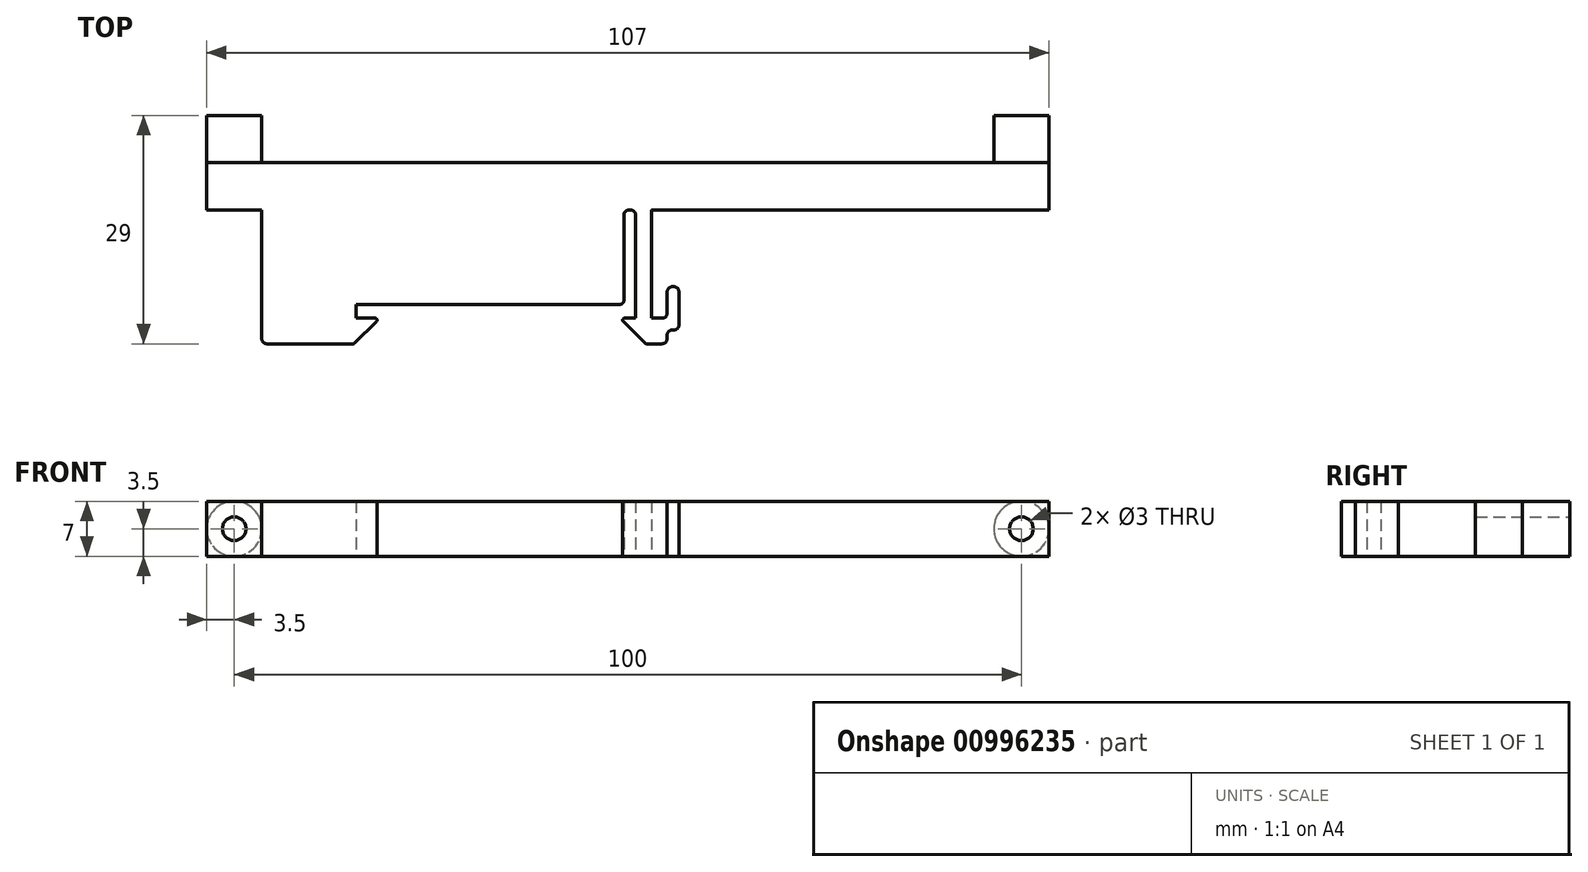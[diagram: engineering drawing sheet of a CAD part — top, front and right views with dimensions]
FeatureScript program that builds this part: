
annotation { "Feature Type Name" : "Feature", "Feature Type Description" : "" }
export const myFeature = defineFeature(function(context is Context, id is Id, definition is map)
    precondition{}
    {
        {
            var Q0;
            Q0=qCreatedBy(makeId("Top.planeOp"),FACE);
            var sketch = newSketch(context, id + "F0", { "sketchPlane" : qUnion([Q0])});
            skLineSegment(sketch, "E0", {"start": v(0, 0) * mm, "end": v(33.5, 0) * mm});
            skLineSegment(sketch, "E1", {"start": v(34, 0.5) * mm, "end": v(34, 11.35) * mm});
            skLineSegment(sketch, "E2", {"start": v(34.65, 12) * mm, "end": v(34.85, 12) * mm});
            skLineSegment(sketch, "E3", {"start": v(35.5, 11.35) * mm, "end": v(35.5, -1.75) * mm});
            skLineSegment(sketch, "E4", {"start": v(35.5, -1.75) * mm, "end": v(34.1, -1.75) * mm});
            skLineSegment(sketch, "E5", {"start": v(33.93, -2.18) * mm, "end": v(36.68, -4.93) * mm});
            skLineSegment(sketch, "E6", {"start": v(36.85, -5) * mm, "end": v(38.85, -5) * mm});
            skLineSegment(sketch, "E7", {"start": v(39.5, -4.35) * mm, "end": v(39.5, -3.9) * mm});
            skLineSegment(sketch, "E8", {"start": v(40.15, -3.25) * mm, "end": v(40.35, -3.25) * mm});
            skLineSegment(sketch, "E9", {"start": v(41, -2.6) * mm, "end": v(41, 1.6) * mm});
            skLineSegment(sketch, "E10", {"start": v(40.35, 2.25) * mm, "end": v(40.15, 2.25) * mm});
            skLineSegment(sketch, "E11", {"start": v(39.5, 1.6) * mm, "end": v(39.5, -1.1) * mm});
            skLineSegment(sketch, "E12", {"start": v(38.85, -1.75) * mm, "end": v(37.5, -1.75) * mm});
            skLineSegment(sketch, "E13", {"start": v(37.5, -1.75) * mm, "end": v(37.5, 11.96) * mm});
            skLineSegment(sketch, "E14", {"start": v(37.54, 12) * mm, "end": v(88, 12) * mm});
            skLineSegment(sketch, "E15", {"start": v(88, 12) * mm, "end": v(88, 18) * mm});
            skLineSegment(sketch, "E16", {"start": v(88, 18) * mm, "end": v(-19, 18) * mm});
            skLineSegment(sketch, "E17", {"start": v(-19, 18) * mm, "end": v(-19, 12) * mm});
            skLineSegment(sketch, "E18", {"start": v(-19, 12) * mm, "end": v(-12, 12) * mm});
            skLineSegment(sketch, "E19", {"start": v(-12, 12) * mm, "end": v(-12, -4.35) * mm});
            skLineSegment(sketch, "E20", {"start": v(-11.35, -5) * mm, "end": v(-0.35, -5) * mm});
            skLineSegment(sketch, "E21", {"start": v(-0.18, -4.93) * mm, "end": v(2.57, -2.18) * mm});
            skLineSegment(sketch, "E22", {"start": v(2.4, -1.75) * mm, "end": v(0, -1.75) * mm});
            skLineSegment(sketch, "E23", {"start": v(0, -1.75) * mm, "end": v(0, 0) * mm});
            skPoint(sketch, "E24.visualSharp", {"position": v(-0.25, -5) * mm});
            skArc(sketch, "E24.filletArc", {"start": v(-0.35, -5) * mm, "mid": v(-0.26, -4.98) * mm, "end": v(-0.18, -4.93) * mm});
            skPoint(sketch, "E25.visualSharp", {"position": v(3, -1.75) * mm});
            skArc(sketch, "E25.filletArc", {"start": v(2.57, -2.18) * mm, "mid": v(2.63, -1.9) * mm, "end": v(2.4, -1.75) * mm});
            skPoint(sketch, "E26.visualSharp", {"position": v(33.5, -1.75) * mm});
            skArc(sketch, "E26.filletArc", {"start": v(34.1, -1.75) * mm, "mid": v(33.87, -1.9) * mm, "end": v(33.93, -2.18) * mm});
            skPoint(sketch, "E27.visualSharp", {"position": v(36.75, -5) * mm});
            skArc(sketch, "E27.filletArc", {"start": v(36.68, -4.93) * mm, "mid": v(36.76, -4.98) * mm, "end": v(36.85, -5) * mm});
            skPoint(sketch, "E28.visualSharp", {"position": v(34, 12) * mm});
            skArc(sketch, "E28.filletArc", {"start": v(34.65, 12) * mm, "mid": v(34.2, 11.8) * mm, "end": v(34, 11.35) * mm});
            skPoint(sketch, "E29.visualSharp", {"position": v(35.5, 12) * mm});
            skArc(sketch, "E29.filletArc", {"start": v(35.5, 11.35) * mm, "mid": v(35.3, 11.8) * mm, "end": v(34.85, 12) * mm});
            skPoint(sketch, "E30.visualSharp", {"position": v(-12, -5) * mm});
            skArc(sketch, "E30.filletArc", {"start": v(-12, -4.35) * mm, "mid": v(-11.8, -4.8) * mm, "end": v(-11.35, -5) * mm});
            skPoint(sketch, "E31.visualSharp", {"position": v(39.5, -5) * mm});
            skArc(sketch, "E31.filletArc", {"start": v(38.85, -5) * mm, "mid": v(39.3, -4.8) * mm, "end": v(39.5, -4.35) * mm});
            skPoint(sketch, "E32.visualSharp", {"position": v(39.5, -3.25) * mm});
            skArc(sketch, "E32.filletArc", {"start": v(40.15, -3.25) * mm, "mid": v(39.7, -3.44) * mm, "end": v(39.5, -3.9) * mm});
            skPoint(sketch, "E33.visualSharp", {"position": v(41, -3.25) * mm});
            skArc(sketch, "E33.filletArc", {"start": v(40.35, -3.25) * mm, "mid": v(40.8, -3.06) * mm, "end": v(41, -2.6) * mm});
            skPoint(sketch, "E34.visualSharp", {"position": v(39.5, -1.75) * mm});
            skArc(sketch, "E34.filletArc", {"start": v(38.85, -1.75) * mm, "mid": v(39.3, -1.56) * mm, "end": v(39.5, -1.1) * mm});
            skPoint(sketch, "E35.visualSharp", {"position": v(41, 2.25) * mm});
            skArc(sketch, "E35.filletArc", {"start": v(41, 1.6) * mm, "mid": v(40.8, 2.06) * mm, "end": v(40.35, 2.25) * mm});
            skPoint(sketch, "E36.visualSharp", {"position": v(39.5, 2.25) * mm});
            skArc(sketch, "E36.filletArc", {"start": v(40.15, 2.25) * mm, "mid": v(39.7, 2.06) * mm, "end": v(39.5, 1.6) * mm});
            skPoint(sketch, "E37.visualSharp", {"position": v(34, 0) * mm});
            skArc(sketch, "E37.filletArc", {"start": v(33.5, 0) * mm, "mid": v(33.85, 0.15) * mm, "end": v(34, 0.5) * mm});
            skPoint(sketch, "E38.visualSharp", {"position": v(37.5, 12) * mm});
            skArc(sketch, "E38.filletArc", {"start": v(37.54, 12) * mm, "mid": v(37.51, 11.99) * mm, "end": v(37.5, 11.96) * mm});
            skSolve(sketch);
        }
        {
            var Q0;
            Q0=qSketchRegion(id+"F0",true);
            extrude(context, id + "F1", {"entities" : qUnion([Q0]), "depth" : 7 * mm, "offsetDistance" : 25 * mm, "symmetric" : true});
        }
        {
            var Q0;
            Q0=makeQuery(id+"F1.opExtrude","SWEPT_FACE",FACE,{"disambiguationData":[OSD([sQuery(id+"F0.wireOp",EDGE,"E16")])]});
            var sketch = newSketch(context, id + "F2", { "sketchPlane" : qUnion([Q0])});
            skCircle(sketch, "E39", {"center": v(-84.5, 0) * mm, "radius": 3.5 * mm});
            skCircle(sketch, "E40", {"center": v(15.5, 0) * mm, "radius": 3.5 * mm});
            skSolve(sketch);
        }
        {
            var Q0;
            Q0=qSketchRegion(id+"F2",true);
            extrude(context, id + "F3", {"entities" : qUnion([Q0]), "operationType" : NewBodyOperationType.ADD, "depth" : 6 * mm, "offsetDistance" : 25 * mm});
        }
        {
            var Q0;
            Q0=makeQuery(id+"F3.opExtrude","CAP_FACE",FACE,{"disambiguationData":[OSD([sQuery(id+"F2.wireOp",EDGE,"E39")])],"isStart":false});
            var sketch = newSketch(context, id + "F4", { "sketchPlane" : qUnion([Q0])});
            skCircle(sketch, "E41", {"center": v(-84.5, 0) * mm, "radius": 1.5 * mm});
            skCircle(sketch, "E42", {"center": v(15.5, 0) * mm, "radius": 1.5 * mm});
            skSolve(sketch);
        }
        {
            var Q0;
            Q0=qSketchRegion(id+"F4",true);
            extrude(context, id + "F5", {"entities" : qUnion([Q0]), "operationType" : NewBodyOperationType.REMOVE, "endBound" : BoundingType.THROUGH_ALL, "oppositeDirection" : true, "depth" : 25 * mm, "offsetDistance" : 25 * mm});
        }
    });
